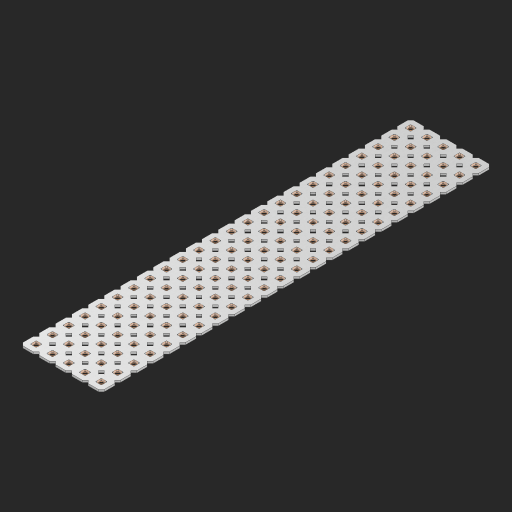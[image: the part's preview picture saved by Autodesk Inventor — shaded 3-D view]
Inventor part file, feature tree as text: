
AUTODESK INVENTOR PART (.ipt)
format: ipt  version: 2023 (Build 270158000, 158)  size: 1,669,632 bytes
history: native  units: in
note: dims shown in document units (in); Inventor stores cm internally (conversion verified against a paired STEP export)
features: other x121, extrude x119, sketch x2, pattern_linear x1
ambient origin geometry x8: Origin, YZ Plane, XZ Plane, XY Plane, X Axis, Y Axis, Z Axis, Center Point
bodies: Solid1 (feature_tree), Body (feature_tree)
feature tree (243):
  pattern_linear  "Rectangular Pattern1"  Spacing1=0.09in  [1 undecoded]
  sketch  "Sketch1"  dims[d1=0.5in]
  sketch  "Sketch2"  dims[d2=0.182in d3=0.09in d4=0.09in d5=0.09in d6=0.09in d7=0.09in d8=0.09in d9=0.09in d10=0.09in d11=0.02in d13=0.0in d14=0.172in d15=0.0625in d16=0.0in d19=0.5in d22=0.5in]
  other  "Srf1"
  other  "Srf126"
  other  "Srf127"
  other  "Srf128"
  other  "Srf129"
  other  "Srf130"
  other  "Srf131"
  other  "Srf250"
  other  "Srf251"
  other  "Srf252"
  other  "Srf253"
  other  "Srf254"
  other  "Srf255"
  other  "Srf256"
  other  "Srf257"
  other  "Srf258"
  other  "Srf259"
  other  "Srf260"
  other  "Srf261"
  other  "Srf262"
  other  "Srf263"
  other  "Srf264"
  other  "Srf265"
  other  "Srf266"
  other  "Srf268"
  other  "Srf269"
  other  "Srf270"
  other  "Srf271"
  other  "Srf272"
  other  "Srf273"
  other  "Srf274"
  other  "Srf275"
  other  "Srf276"
  other  "Srf277"
  other  "Srf278"
  other  "Srf279"
  other  "Srf280"
  other  "Srf281"
  other  "Srf282"
  other  "Srf283"
  other  "Srf284"
  other  "Srf285"
  other  "Srf286"
  other  "Srf287"
  other  "Srf288"
  other  "Srf289"
  other  "Srf290"
  other  "Srf291"
  other  "Srf293"
  other  "Srf294"
  other  "Srf295"
  other  "Srf296"
  other  "Srf297"
  other  "Srf298"
  other  "Srf299"
  other  "Srf300"
  other  "Srf301"
  other  "Srf302"
  other  "Srf303"
  other  "Srf304"
  other  "Srf305"
  other  "Srf306"
  other  "Srf307"
  other  "Srf308"
  other  "Srf309"
  other  "Srf310"
  other  "Srf311"
  other  "Srf312"
  other  "Srf313"
  other  "Srf314"
  other  "Srf315"
  other  "Srf316"
  other  "Srf318"
  other  "Srf319"
  other  "Srf320"
  other  "Srf321"
  other  "Srf322"
  other  "Srf323"
  other  "Srf324"
  other  "Srf325"
  other  "Srf326"
  other  "Srf327"
  other  "Srf328"
  other  "Srf329"
  other  "Srf330"
  other  "Srf331"
  other  "Srf332"
  other  "Srf333"
  other  "Srf334"
  other  "Srf335"
  other  "Srf336"
  other  "Srf337"
  other  "Srf338"
  other  "Srf339"
  other  "Srf340"
  other  "Srf341"
  other  "Srf343"
  other  "Srf344"
  other  "Srf345"
  other  "Srf346"
  other  "Srf347"
  other  "Srf348"
  other  "Srf349"
  other  "Srf350"
  other  "Srf351"
  other  "Srf352"
  other  "Srf353"
  other  "Srf354"
  other  "Srf355"
  other  "Srf356"
  other  "Srf357"
  other  "Srf358"
  other  "Srf359"
  other  "Srf360"
  other  "Srf361"
  other  "Srf362"
  other  "Srf363"
  other  "Srf364"
  other  "Srf365"
  other  "Srf366"
  other  "Circle"
  extrude  "ExtrusionSrf126"  Depth=0.09in
  extrude  "ExtrusionSrf127"  Depth=0.09in
  extrude  "ExtrusionSrf128"  Depth=0.09in
  extrude  "ExtrusionSrf129"  Depth=0.09in
  extrude  "ExtrusionSrf130"  Depth=0.09in
  extrude  "ExtrusionSrf131"  Depth=0.09in
  extrude  "ExtrusionSrf250"  Depth=0.09in
  extrude  "ExtrusionSrf251"  Depth=0.02in
  extrude  "ExtrusionSrf252"  TaperAngle=0.0deg  [1 undecoded]
  extrude  "ExtrusionSrf253"  Depth=0.5in
  extrude  "ExtrusionSrf254"  Depth=0.0625in TaperAngle=0.0deg
  extrude  "ExtrusionSrf255"  Depth=0.5in
  extrude  "ExtrusionSrf256"  Depth=0.5in
  extrude  "ExtrusionSrf257"  [1 undecoded]
  extrude  "ExtrusionSrf258"  [1 undecoded]
  extrude  "ExtrusionSrf259"  [1 undecoded]
  extrude  "ExtrusionSrf260"  [1 undecoded]
  extrude  "ExtrusionSrf261"  [1 undecoded]
  extrude  "ExtrusionSrf262"  [1 undecoded]
  extrude  "ExtrusionSrf263"  [1 undecoded]
  extrude  "ExtrusionSrf264"  [1 undecoded]
  extrude  "ExtrusionSrf265"  [1 undecoded]
  extrude  "ExtrusionSrf266"  [1 undecoded]
  extrude  "ExtrusionSrf268"  [1 undecoded]
  extrude  "ExtrusionSrf269"  [1 undecoded]
  extrude  "ExtrusionSrf270"  [1 undecoded]
  extrude  "ExtrusionSrf271"  [1 undecoded]
  extrude  "ExtrusionSrf272"  [1 undecoded]
  extrude  "ExtrusionSrf273"  [1 undecoded]
  extrude  "ExtrusionSrf274"  [1 undecoded]
  extrude  "ExtrusionSrf275"  [1 undecoded]
  extrude  "ExtrusionSrf276"  [1 undecoded]
  extrude  "ExtrusionSrf277"  [1 undecoded]
  extrude  "ExtrusionSrf278"  [1 undecoded]
  extrude  "ExtrusionSrf279"  [1 undecoded]
  extrude  "ExtrusionSrf280"  [1 undecoded]
  extrude  "ExtrusionSrf281"  [1 undecoded]
  extrude  "ExtrusionSrf282"  [1 undecoded]
  extrude  "ExtrusionSrf283"  [1 undecoded]
  extrude  "ExtrusionSrf284"  [1 undecoded]
  extrude  "ExtrusionSrf285"  [1 undecoded]
  extrude  "ExtrusionSrf286"  [1 undecoded]
  extrude  "ExtrusionSrf287"  [1 undecoded]
  extrude  "ExtrusionSrf288"  [1 undecoded]
  extrude  "ExtrusionSrf289"  [1 undecoded]
  extrude  "ExtrusionSrf290"  [1 undecoded]
  extrude  "ExtrusionSrf291"  [1 undecoded]
  extrude  "ExtrusionSrf293"  [1 undecoded]
  extrude  "ExtrusionSrf294"  [1 undecoded]
  extrude  "ExtrusionSrf295"  [1 undecoded]
  extrude  "ExtrusionSrf296"  [1 undecoded]
  extrude  "ExtrusionSrf297"  [1 undecoded]
  extrude  "ExtrusionSrf298"  [1 undecoded]
  extrude  "ExtrusionSrf299"  [1 undecoded]
  extrude  "ExtrusionSrf300"  [1 undecoded]
  extrude  "ExtrusionSrf301"  [1 undecoded]
  extrude  "ExtrusionSrf302"  [1 undecoded]
  extrude  "ExtrusionSrf303"  [1 undecoded]
  extrude  "ExtrusionSrf304"  [1 undecoded]
  extrude  "ExtrusionSrf305"  [1 undecoded]
  extrude  "ExtrusionSrf306"  [1 undecoded]
  extrude  "ExtrusionSrf307"  [1 undecoded]
  extrude  "ExtrusionSrf308"  [1 undecoded]
  extrude  "ExtrusionSrf309"  [1 undecoded]
  extrude  "ExtrusionSrf310"  [1 undecoded]
  extrude  "ExtrusionSrf311"  [1 undecoded]
  extrude  "ExtrusionSrf312"  [1 undecoded]
  extrude  "ExtrusionSrf313"  [1 undecoded]
  extrude  "ExtrusionSrf314"  [1 undecoded]
  extrude  "ExtrusionSrf315"  [1 undecoded]
  extrude  "ExtrusionSrf316"  [1 undecoded]
  extrude  "ExtrusionSrf318"  [1 undecoded]
  extrude  "ExtrusionSrf319"  [1 undecoded]
  extrude  "ExtrusionSrf320"  [1 undecoded]
  extrude  "ExtrusionSrf321"  [1 undecoded]
  extrude  "ExtrusionSrf322"  [1 undecoded]
  extrude  "ExtrusionSrf323"  [1 undecoded]
  extrude  "ExtrusionSrf324"  [1 undecoded]
  extrude  "ExtrusionSrf325"  [1 undecoded]
  extrude  "ExtrusionSrf326"  [1 undecoded]
  extrude  "ExtrusionSrf327"  [1 undecoded]
  extrude  "ExtrusionSrf328"  [1 undecoded]
  extrude  "ExtrusionSrf329"  [1 undecoded]
  extrude  "ExtrusionSrf330"  [1 undecoded]
  extrude  "ExtrusionSrf331"  [1 undecoded]
  extrude  "ExtrusionSrf332"  [1 undecoded]
  extrude  "ExtrusionSrf333"  [1 undecoded]
  extrude  "ExtrusionSrf334"  [1 undecoded]
  extrude  "ExtrusionSrf335"  [1 undecoded]
  extrude  "ExtrusionSrf336"  [1 undecoded]
  extrude  "ExtrusionSrf337"  [1 undecoded]
  extrude  "ExtrusionSrf338"  [1 undecoded]
  extrude  "ExtrusionSrf339"  [1 undecoded]
  extrude  "ExtrusionSrf340"  [1 undecoded]
  extrude  "ExtrusionSrf341"  [1 undecoded]
  extrude  "ExtrusionSrf343"  [1 undecoded]
  extrude  "ExtrusionSrf344"  [1 undecoded]
  extrude  "ExtrusionSrf345"  [1 undecoded]
  extrude  "ExtrusionSrf346"  [1 undecoded]
  extrude  "ExtrusionSrf347"  [1 undecoded]
  extrude  "ExtrusionSrf348"  [1 undecoded]
  extrude  "ExtrusionSrf349"  [1 undecoded]
  extrude  "ExtrusionSrf350"  [1 undecoded]
  extrude  "ExtrusionSrf351"  [1 undecoded]
  extrude  "ExtrusionSrf352"  [1 undecoded]
  extrude  "ExtrusionSrf353"  [1 undecoded]
  extrude  "ExtrusionSrf354"  [1 undecoded]
  extrude  "ExtrusionSrf355"  [1 undecoded]
  extrude  "ExtrusionSrf356"  [1 undecoded]
  extrude  "ExtrusionSrf357"  [1 undecoded]
  extrude  "ExtrusionSrf358"  [1 undecoded]
  extrude  "ExtrusionSrf359"  [1 undecoded]
  extrude  "ExtrusionSrf360"  [1 undecoded]
  extrude  "ExtrusionSrf361"  [1 undecoded]
  extrude  "ExtrusionSrf362"  [1 undecoded]
  extrude  "ExtrusionSrf363"  [1 undecoded]
  extrude  "ExtrusionSrf364"  [1 undecoded]
  extrude  "ExtrusionSrf365"  [1 undecoded]
  extrude  "ExtrusionSrf366"  [1 undecoded]
note: 108 required parameter values undecoded (feature->parameter linkage not recoverable at this tier; creation-order binding heuristic only, values carry confidence <= 0.55)
